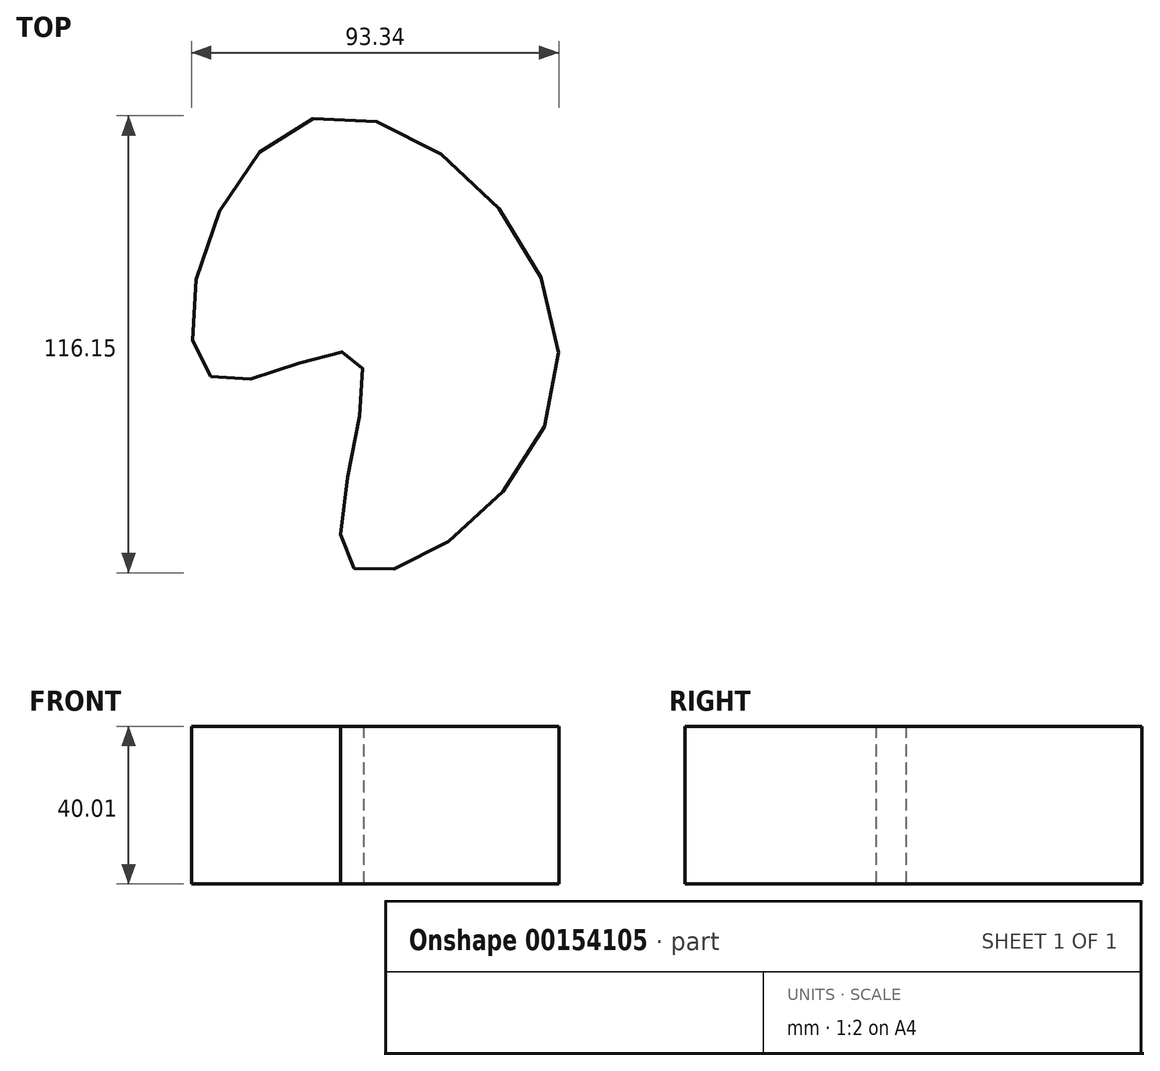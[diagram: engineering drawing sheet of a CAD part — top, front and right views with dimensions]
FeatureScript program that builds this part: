
annotation { "Feature Type Name" : "Feature", "Feature Type Description" : "" }
export const myFeature = defineFeature(function(context is Context, id is Id, definition is map)
    precondition{}
    {
        {
            var Q0;
            Q0=qCreatedBy(makeId("Top.planeOp"),FACE);
            var sketch = newSketch(context, id + "F0", { "sketchPlane" : qUnion([Q0])});
            skFitSpline(sketch, "E0", {"points": [v(-41.9, -21.47) * mm, v(-18.85, 43.1) * mm, v(46.17, -22.5) * mm, v(-6.98, -68.88) * mm, v(-4.75, -16.32) * mm, v(-41.9, -21.47) * mm]});
            skSolve(sketch);
        }
        {
            var Q0;
            Q0=makeQuery(id+"F0.imprint","IMPRINT",FACE,{"disambiguationData":[TD([[makeQuery(id+"F0.imprint","IMPRINT",EDGE,{"derivedFrom":sQuery(id+"F0.wireOp",EDGE,"E0")}),-1.0]])]});
            extrude(context, id + "F1", {"entities" : qUnion([Q0]), "depth" : 40 * mm});
        }
    });
